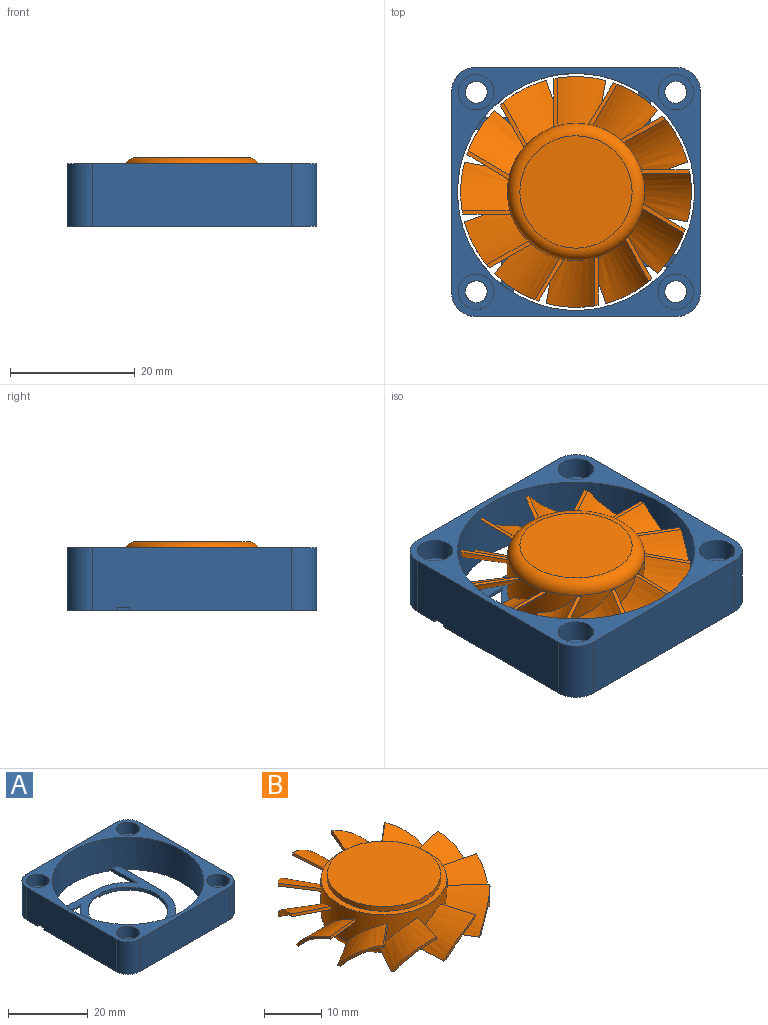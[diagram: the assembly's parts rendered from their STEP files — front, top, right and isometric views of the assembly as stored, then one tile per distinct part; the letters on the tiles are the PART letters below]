
ASSEMBLY  parts=2 mates=1
PART A: 42 faces, bbox 40.8x40.8x10.8 mm
  f0: plane 6.46x6.46mm, normal (0,0,1), area 16mm2, adj f7,f8
  f1: plane 6.46x6.46mm, normal (0,0,1), area 16mm2, adj f6,f9
  f2: plane 6.46x6.46mm, normal (0,0,1), area 16mm2, adj f5,f10
  f3: plane 6.46x6.46mm, normal (0,0,1), area 16mm2, adj f4,f11
  f4: cylinder r=2.85mm len=5.7mm, axis (0,0,-1), area 62.7mm2, adj f3,f37
  f5: cylinder r=2.85mm len=5.7mm, axis (0,0,-1), area 62.7mm2, adj f2,f37
  f6: cylinder r=2.85mm len=5.7mm, axis (0,0,-1), area 62.7mm2, adj f1,f37
  f7: cylinder r=2.85mm len=5.7mm, axis (0,0,-1), area 62.7mm2, adj f0,f37
  f8: cylinder r=1.75mm len=6.5mm, axis (0,0,-1), area 71.5mm2, adj f0,f39
  f9: cylinder r=1.75mm len=6.5mm, axis (0,0,-1), area 71.5mm2, adj f1,f39
  f10: cylinder r=1.75mm len=6.5mm, axis (0,0,-1), area 71.5mm2, adj f2,f39
  f11: cylinder r=1.75mm len=6.5mm, axis (0,0,-1), area 71.5mm2, adj f3,f39
  f12: cylinder r=4mm len=10mm, axis (0,0,-1), area 62.8mm2, adj f22,f23,f37,f39
  f13: cylinder r=4mm len=10mm, axis (0,0,-1), area 62.8mm2, adj f23,f24,f37,f39
  f14: cylinder r=12mm len=10mm, axis (0,0,-1), area 11.8mm2, adj f18,f20,f25,f26,f39
  f15: cylinder r=10mm len=20mm, axis (0,0,1), area 59.2mm2, adj f18,f26,f27,f34,f39
  f16: cylinder r=12mm len=10mm, axis (0,0,-1), area 11.8mm2, adj f18,f21,f27,f28,f39
  f17: cylinder r=12mm len=10mm, axis (0,0,-1), area 11.8mm2, adj f18,f29,f30,f39
  f18: plane 32.4x32.4mm, normal (0,0,1), area 224.9mm2, adj f14,f15,f16,f17,f19,f20,f21,f25
  f19: cylinder r=12mm len=10mm, axis (0,0,-1), area 11.8mm2, adj f18,f31,f32,f39
  f20: plane 9.52x0.5mm, normal (0,-1,0), area 4.8mm2, adj f14,f18,f33,f34
  f21: plane 14.73x0.5mm, normal (0,1,0), area 7.4mm2, adj f16,f18,f33,f34
  f22: plane 32x10mm, normal (0,1,0), area 320mm2, adj f12,f37,f38,f39
  f23: plane 32x10mm, normal (1,0,0), area 320mm2, adj f12,f13,f37,f39
  f24: plane 32x10mm, normal (0,-1,0), area 320mm2, adj f13,f36,f37,f39
  f25: plane 14.73x1mm, normal (-1,0,0), area 14.7mm2, adj f14,f18,f33,f39
  f26: plane 2.52x0.5mm, normal (1,0,0), area 1.3mm2, adj f14,f15,f34,f39
  f27: plane 2x0.5mm, normal (-1,0,0), area 1mm2, adj f15,f16,f34,f39
  f28: plane 9.52x1mm, normal (-1,0,0), area 9.5mm2, adj f16,f18,f33,f39
  f29: plane 14.73x1mm, normal (1,0,0), area 14.7mm2, adj f17,f18,f33,f39
  f30: plane 9.52x1mm, normal (0,1,0), area 9.5mm2, adj f17,f18,f33,f39
  f31: plane 9.52x1mm, normal (1,0,0), area 9.5mm2, adj f18,f19,f33,f39
  f32: plane 14.73x1mm, normal (0,-1,0), area 14.7mm2, adj f18,f19,f33,f39
  f33: cylinder r=19mm len=38mm, axis (0,0,1), area 1184mm2, adj f18,f20,f21,f25,f28,f29,f30,f31
  f34: plane 20.07x4.59mm, normal (0,0,-1), area 45.2mm2, adj f15,f20,f21,f26,f27,f35,f40,f41
  f35: plane 3.84x0.5mm, normal (0,1,0), area 1.9mm2, adj f33,f34,f39,f41
  f36: cylinder r=4mm len=10mm, axis (0,0,-1), area 62.8mm2, adj f24,f37,f39,f41
  f37: plane 40.12x40.12mm, normal (0,0,1), area 350.4mm2, adj f4,f5,f6,f7,f12,f13,f22,f23
  f38: cylinder r=4mm len=10mm, axis (0,0,-1), area 62.8mm2, adj f22,f37,f39,f41
  f39: plane 40.02x40.02mm, normal (0,0,-1), area 752.4mm2, adj f8,f9,f10,f11,f12,f13,f14,f15
  f40: plane 5.27x0.5mm, normal (0,-1,0), area 2.6mm2, adj f33,f34,f39,f41
  f41: plane 32x10mm, normal (-1,0,0), area 319mm2, adj f34,f35,f36,f37,f38,f39,f40
PART B: 78 faces, bbox 47x47x10.7 mm
  f0: plane 19.83x19.83mm, normal (0,0,1), area 307.3mm2, adj f1
  f1: cylinder r=9.9mm len=19.8mm, axis (0,0,-1), area 62.2mm2, adj f0,f3
  f2: plane 18x18mm, normal (0,0,-1), area 253.9mm2, adj f45
  f3: plane 22.09x22.09mm, normal (0,0,1), area 71mm2, adj f1,f75
  f4: plane 8.6x1.46mm, normal (0,0,-1), area 4.9mm2, adj f15,f46,f47,f48,f75
  f5: plane 7.91x4.96mm, normal (0,0,-1), area 4.9mm2, adj f16,f17,f50,f51,f75
  f6: plane 8.6x1.46mm, normal (0,0,-1), area 4.9mm2, adj f18,f19,f20,f53,f75
  f7: plane 7.54x5.29mm, normal (0,0,-1), area 4.9mm2, adj f21,f22,f23,f55,f75
  f8: plane 7.91x4.96mm, normal (0,0,-1), area 4.9mm2, adj f24,f25,f26,f57,f75
  f9: plane 8.61x1.46mm, normal (0,0,-1), area 4.9mm2, adj f27,f28,f29,f59,f75
  f10: plane 7.54x5.29mm, normal (0,0,-1), area 4.9mm2, adj f30,f31,f61,f62,f75
  f11: plane 7.91x4.96mm, normal (0,0,-1), area 4.9mm2, adj f32,f33,f64,f65,f75
  f12: plane 8.6x1.46mm, normal (0,0,-1), area 4.9mm2, adj f34,f35,f36,f67,f75
  f13: plane 7.54x5.29mm, normal (0,0,-1), area 4.9mm2, adj f37,f38,f39,f69,f75
  f14: plane 7.91x4.96mm, normal (0,0,-1), area 4.9mm2, adj f40,f41,f42,f71,f75
  f15: cylinder r=18.5mm len=8.32mm, axis (0,0,-1), area 5mm2, adj f4,f44,f46,f48
  f16: offset ~17.14x13.81mm, area 71.7mm2, adj f5,f17,f51,f52,f75
  f17: cylinder r=18.5mm len=7.34mm, axis (0,0,-1), area 5mm2, adj f5,f16,f50,f52
  f18: offset ~14.46x10.29mm, area 71.7mm2, adj f6,f19,f53,f54,f75
  f19: cylinder r=18.5mm len=8.32mm, axis (0,0,-1), area 5mm2, adj f6,f18,f20,f54
  f20: offset ~12.66x9.93mm, area 66.2mm2, adj f6,f19,f54,f75
  f21: offset ~16.23x15.39mm, area 71.7mm2, adj f7,f22,f55,f56,f75
  f22: cylinder r=18.5mm len=7.06mm, axis (0,0,-1), area 5mm2, adj f7,f21,f23,f56
  f23: offset ~14.68x14.27mm, area 66.2mm2, adj f7,f22,f56,f75
  f24: offset ~17.14x13.81mm, area 71.7mm2, adj f8,f25,f57,f58,f75
  f25: cylinder r=18.5mm len=7.34mm, axis (0,0,-1), area 5mm2, adj f8,f24,f26,f58
  f26: offset ~15.47x12.9mm, area 66.2mm2, adj f8,f25,f58,f75
  f27: offset ~14.46x10.29mm, area 71.7mm2, adj f9,f28,f59,f60,f75
  f28: cylinder r=18.5mm len=8.32mm, axis (0,0,-1), area 5mm2, adj f9,f27,f29,f60
  f29: offset ~12.66x9.93mm, area 66.2mm2, adj f9,f28,f60,f75
  f30: offset ~16.23x15.39mm, area 71.7mm2, adj f10,f31,f62,f63,f75
  f31: cylinder r=18.5mm len=7.06mm, axis (0,0,-1), area 5mm2, adj f10,f30,f61,f63
  f32: offset ~17.14x13.81mm, area 71.7mm2, adj f11,f33,f65,f66,f75
  f33: cylinder r=18.5mm len=7.34mm, axis (0,0,-1), area 5mm2, adj f11,f32,f64,f66
  f34: offset ~14.46x10.29mm, area 71.7mm2, adj f12,f35,f67,f68,f75
  f35: cylinder r=18.5mm len=8.32mm, axis (0,0,-1), area 5mm2, adj f12,f34,f36,f68
  f36: offset ~12.66x9.93mm, area 66.2mm2, adj f12,f35,f68,f75
  f37: offset ~16.23x15.39mm, area 71.7mm2, adj f13,f38,f69,f70,f75
  f38: cylinder r=18.5mm len=7.06mm, axis (0,0,-1), area 5mm2, adj f13,f37,f39,f70
  f39: offset ~14.68x14.27mm, area 66.2mm2, adj f13,f38,f70,f75
  f40: offset ~17.14x13.81mm, area 71.7mm2, adj f14,f41,f71,f72,f75
  f41: cylinder r=18.5mm len=7.34mm, axis (0,0,-1), area 5mm2, adj f14,f40,f42,f72
  f42: offset ~15.47x12.9mm, area 66.2mm2, adj f14,f41,f72,f75
  f43: plane 7.54x5.29mm, normal (0,0,-1), area 4.9mm2, adj f49,f73,f74,f75,f77
  f44: bspline ~9.04x1.73mm, area 3.8mm2, adj f15,f46,f48,f75
  f45: torus R=9mm, axis (0,0,-1), area 202.6mm2, adj f2,f75
  f46: offset ~12.66x9.93mm, area 64.2mm2, adj f4,f15,f44,f75
  f47: cylinder r=16.24mm len=0.14mm, axis (0.98,0.05,-0.17), area 0mm2, adj f4,f48,f75
  f48: offset ~14.46x10.29mm, area 71.3mm2, adj f4,f15,f44,f47,f75
  f49: cylinder r=16.24mm len=0.13mm, axis (0.82,0.54,-0.17), area 0mm2, adj f43,f73,f75
  f50: offset ~15.47x12.9mm, area 66.2mm2, adj f5,f17,f52,f75
  f51: cylinder r=16.24mm len=0.13mm, axis (0.44,0.88,-0.17), area 0mm2, adj f5,f16,f75
  f52: bspline ~8.7x3.26mm, area 3.8mm2, adj f16,f17,f50,f75
  f53: cylinder r=16.24mm len=0.14mm, axis (-0.05,0.98,-0.17), area 0mm2, adj f6,f18,f75
  f54: bspline ~9.04x1.73mm, area 3.8mm2, adj f18,f19,f20,f75
  f55: cylinder r=16.24mm len=0.13mm, axis (-0.54,0.82,-0.17), area 0mm2, adj f7,f21,f75
  f56: bspline ~7.09x6.02mm, area 3.8mm2, adj f21,f22,f23,f75
  f57: cylinder r=16.25mm len=0.13mm, axis (-0.88,0.44,-0.17), area 0mm2, adj f8,f24
  f58: bspline ~8.7x3.26mm, area 3.8mm2, adj f24,f25,f26,f75
  f59: cylinder r=16.25mm len=0.14mm, axis (-0.98,-0.05,-0.17), area 0mm2, adj f9,f27
  f60: bspline ~9.04x1.73mm, area 3.8mm2, adj f27,f28,f29,f75
  f61: offset ~14.68x14.27mm, area 66.2mm2, adj f10,f31,f63,f75
  f62: cylinder r=16.24mm len=0.13mm, axis (-0.82,-0.54,-0.17), area 0mm2, adj f10,f30,f75
  f63: bspline ~7.09x6.02mm, area 3.8mm2, adj f30,f31,f61,f75
  f64: offset ~15.47x12.9mm, area 66.2mm2, adj f11,f33,f66,f75
  f65: cylinder r=16.24mm len=0.13mm, axis (-0.44,-0.88,-0.17), area 0mm2, adj f11,f32,f75
  f66: bspline ~8.7x3.26mm, area 3.8mm2, adj f32,f33,f64,f75
  f67: cylinder r=16.24mm len=0.14mm, axis (0.05,-0.98,-0.17), area 0mm2, adj f12,f34,f75
  f68: bspline ~9.04x1.73mm, area 3.8mm2, adj f34,f35,f36,f75
  f69: cylinder r=16.24mm len=0.13mm, axis (0.54,-0.82,-0.17), area 0mm2, adj f13,f37,f75
  f70: bspline ~7.09x6.02mm, area 3.8mm2, adj f37,f38,f39,f75
  f71: cylinder r=16.25mm len=0.13mm, axis (0.88,-0.44,-0.17), area 0mm2, adj f14,f40
  f72: bspline ~8.7x3.26mm, area 3.8mm2, adj f40,f41,f42,f75
  f73: offset ~16.23x15.39mm, area 71.7mm2, adj f43,f49,f74,f75,f76
  f74: cylinder r=18.5mm len=7.06mm, axis (0,0,-1), area 5mm2, adj f43,f73,f76,f77
  f75: cylinder r=11mm len=22mm, axis (0,0,-1), area 195.2mm2, adj f3,f4,f5,f6,f7,f8,f9,f10
  f76: bspline ~7.09x6.02mm, area 3.8mm2, adj f73,f74,f75,f77
  f77: offset ~11.35x10.77mm, area 66.2mm2, adj f43,f74,f75,f76
PLACE A t=(43.61,2.86,8.84)mm
PLACE B rot(axis=(0.71,-0.71,0),180deg) t=(23.61,22.86,19.84)mm
MATE fastened B.f38 <-> A.f19  axis (0,0,-1) through (23.61,22.86,9.84)mm
